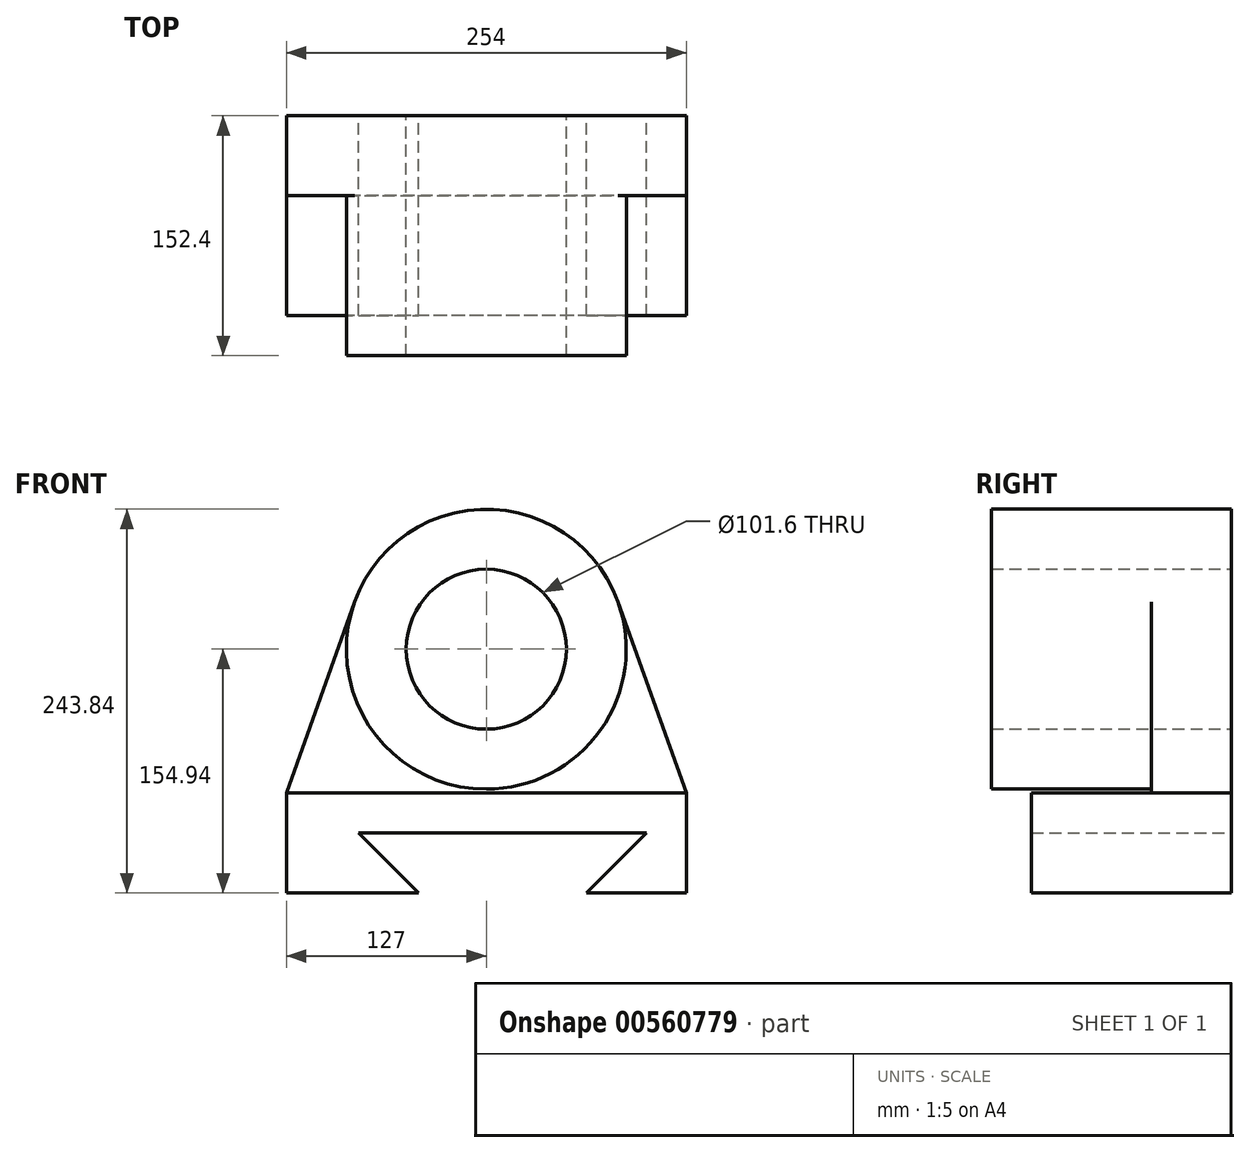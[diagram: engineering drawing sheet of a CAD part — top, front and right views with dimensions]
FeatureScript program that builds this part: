
annotation { "Feature Type Name" : "Feature", "Feature Type Description" : "" }
export const myFeature = defineFeature(function(context is Context, id is Id, definition is map)
    precondition{}
    {
        {
            var Q0;
            Q0=qCreatedBy(makeId("Front.planeOp"),FACE);
            var sketch = newSketch(context, id + "F0", { "sketchPlane" : qUnion([Q0])});
            skLineSegment(sketch, "E0", {"start": v(0, 0) * mm, "end": v(83.86, 0) * mm});
            skLineSegment(sketch, "E1", {"start": v(0, 0) * mm, "end": v(0, 63.5) * mm});
            skCircle(sketch, "E2", {"center": v(127, 154.94) * mm, "radius": 50.8 * mm});
            skCircle(sketch, "E3", {"center": v(127, 154.94) * mm, "radius": 88.9 * mm});
            skLineSegment(sketch, "E4", {"start": v(0, 63.5) * mm, "end": v(43.27, 184.8) * mm});
            skLineSegment(sketch, "E5", {"start": v(254, 0) * mm, "end": v(254, 63.5) * mm});
            skLineSegment(sketch, "E6", {"start": v(254, 63.5) * mm, "end": v(210.73, 184.8) * mm});
            skPoint(sketch, "E7.endSnap0", {"position": v(254, -31.75) * mm});
            skLineSegment(sketch, "E8", {"start": v(254, 63.5) * mm, "end": v(0, 63.5) * mm});
            skLineSegment(sketch, "E9", {"start": v(254, 0) * mm, "end": v(190.5, 0) * mm});
            skLineSegment(sketch, "E10", {"start": v(190.5, 0) * mm, "end": v(228.6, 38.1) * mm});
            skLineSegment(sketch, "E11", {"start": v(228.6, 38.1) * mm, "end": v(45.76, 38.1) * mm});
            skLineSegment(sketch, "E12", {"start": v(45.76, 38.1) * mm, "end": v(83.86, 0) * mm});
            skLineSegment(sketch, "E13.trimOffspring", {"start": v(190.5, 0) * mm, "end": v(254, 0) * mm});
            skPoint(sketch, "E14.end.orphan", {"position": v(254, 154.94) * mm});
            skSolve(sketch);
        }
        {
            var Q0;
            Q0=makeQuery(id+"F0.imprint","IMPRINT",FACE,{"disambiguationData":[TD([[makeQuery(id+"F0.imprint","IMPRINT",EDGE,{"derivedFrom":sQuery(id+"F0.wireOp",EDGE,"E2")}),-1.0]])]});
            extrude(context, id + "F1", {"entities" : qUnion([Q0]), "depth" : 127 * mm, "offsetDistance" : 25.4 * mm});
        }
        {
            var Q0;
            Q0=makeQuery(id+"F1.opExtrude","CAP_FACE",FACE,{"disambiguationData":[OSD([sQuery(id+"F0.wireOp",EDGE,"E2"),sQuery(id+"F0.wireOp",EDGE,"E3")])],"isStart":false});
            extrude(context, id + "F2", {"entities" : qUnion([Q0]), "operationType" : NewBodyOperationType.ADD, "depth" : 25.4 * mm, "offsetDistance" : 25.4 * mm});
        }
        {
            var Q0;
            {var subQ0=sQuery(id+"F0.wireOp",EDGE,"E4");Q0=makeQuery(id+"F0.imprint","IMPRINT",FACE,{"disambiguationData":[TD([[makeQuery(id+"F0.imprint","IMPRINT",EDGE,{"derivedFrom":subQ0}),-1.0]])]});}
            extrude(context, id + "F3", {"entities" : qUnion([Q0]), "operationType" : NewBodyOperationType.ADD, "depth" : 50.8 * mm, "offsetDistance" : 25.4 * mm});
        }
        {
            var Q0;
            Q0=makeQuery(id+"F0.imprint","IMPRINT",FACE,{"disambiguationData":[TD([[makeQuery(id+"F0.imprint","IMPRINT",EDGE,{"derivedFrom":sQuery(id+"F0.wireOp",EDGE,"E0")}),1.0]])]});
            extrude(context, id + "F4", {"entities" : qUnion([Q0]), "operationType" : NewBodyOperationType.ADD, "depth" : 127 * mm, "offsetDistance" : 25.4 * mm});
        }
    });
